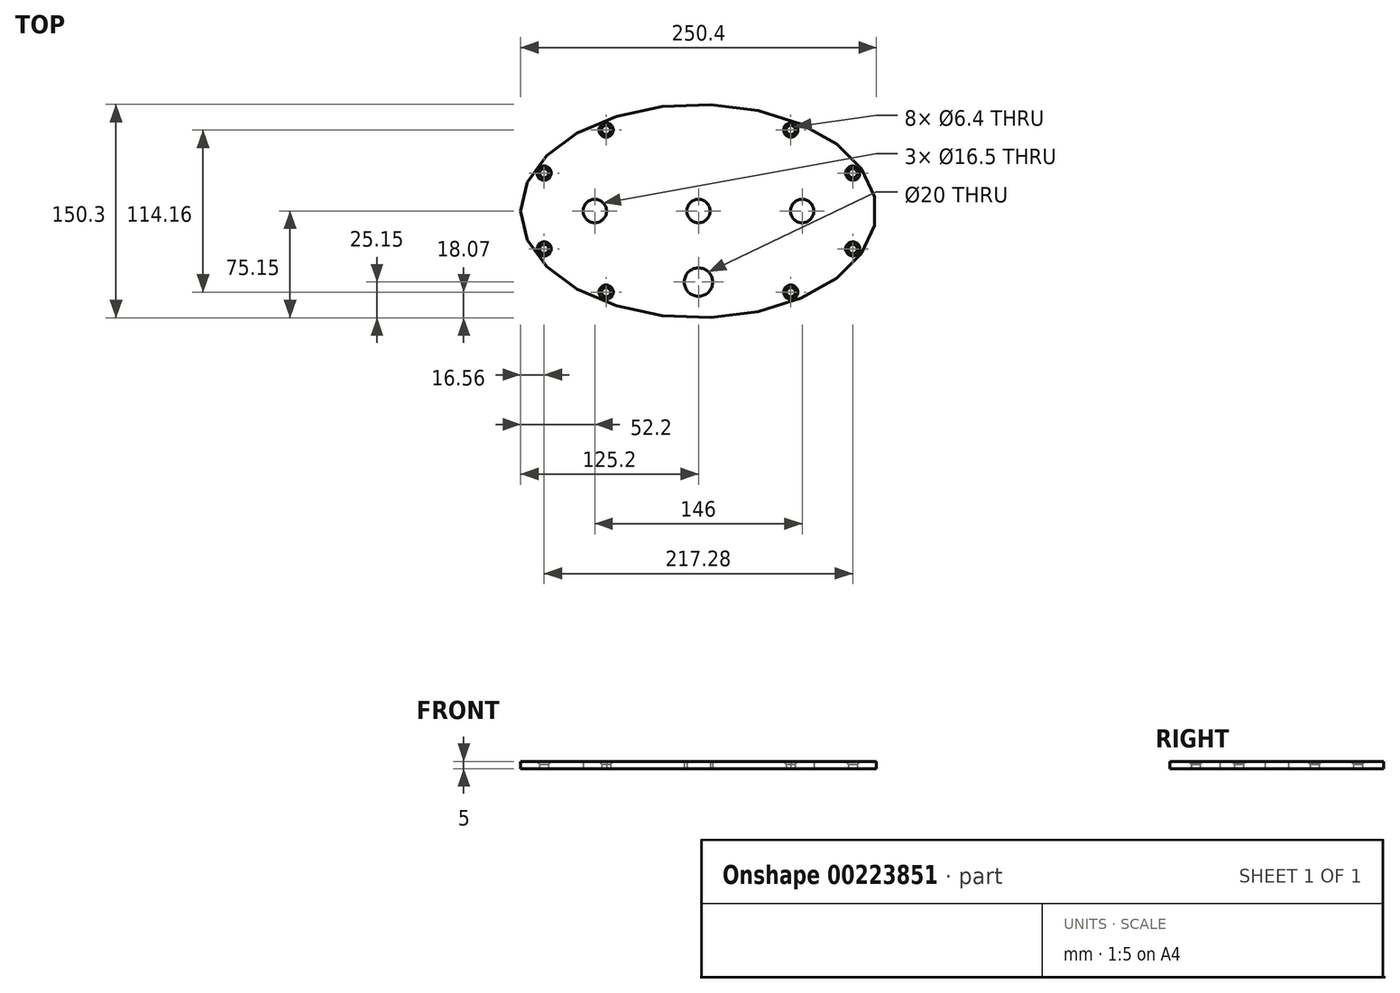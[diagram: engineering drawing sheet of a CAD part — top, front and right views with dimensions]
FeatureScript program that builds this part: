
annotation { "Feature Type Name" : "Feature", "Feature Type Description" : "" }
export const myFeature = defineFeature(function(context is Context, id is Id, definition is map)
    precondition{}
    {
        {
            var Q0;
            Q0=qCreatedBy(makeId("Top.planeOp"),FACE);
            var sketch = newSketch(context, id + "F0", { "sketchPlane" : qUnion([Q0])});
            skEllipse(sketch, "E0", {"center": v(0, 0) * mm, "majorRadius": 125.2 * mm, "minorRadius": 75.15 * mm, "majorAxis": v(-1, 0)});
            skCircle(sketch, "E1", {"center": v(0, 0) * mm, "radius": 8.25 * mm});
            skLineSegment(sketch, "E2", {"start": v(0, 0) * mm, "end": v(-73, 0) * mm});
            skCircle(sketch, "E3", {"center": v(-73, 0) * mm, "radius": 8.25 * mm});
            skCircle(sketch, "E4.MirrorC", {"center": v(73, 0) * mm, "radius": 8.25 * mm});
            skLineSegment(sketch, "E5", {"start": v(0, 0) * mm, "end": v(65, 0) * mm});
            skLineSegment(sketch, "E6", {"start": v(0, 0) * mm, "end": v(73, 0) * mm});
            skLineSegment(sketch, "E7", {"start": v(0, 0) * mm, "end": v(-50, 0) * mm});
            skLineSegment(sketch, "E8", {"start": v(0, -50) * mm, "end": v(0, -50) * mm});
            skCircle(sketch, "E9", {"center": v(0, -50) * mm, "radius": 10 * mm});
            skSolve(sketch);
        }
        {
            var Q0;
            Q0=makeQuery(id+"F0.imprint","IMPRINT",FACE,{"disambiguationData":[TD([[makeQuery(id+"F0.imprint","IMPRINT",EDGE,{"derivedFrom":sQuery(id+"F0.wireOp",EDGE,"E0")}),1.0]])]});
            extrude(context, id + "F1", {"entities" : qUnion([Q0]), "offsetDistance" : 25 * mm, "depth" : 5 * mm});
        }
        {
            var Q0;
            Q0=makeQuery(id+"F1.opExtrude","CAP_FACE",FACE,{"disambiguationData":[OSD([sQuery(id+"F0.wireOp",EDGE,"E0"),sQuery(id+"F0.wireOp",EDGE,"E1"),sQuery(id+"F0.wireOp",EDGE,"E3"),sQuery(id+"F0.wireOp",EDGE,"E4.MirrorC")])],"isStart":false});
            var sketch = newSketch(context, id + "F2", { "sketchPlane" : qUnion([Q0])});
            skLineSegment(sketch, "E10", {"start": v(-65, 0) * mm, "end": v(-65, 57.08) * mm});
            skLineSegment(sketch, "E11.MirrorCS", {"start": v(65, 0) * mm, "end": v(65, 57.08) * mm});
            skLineSegment(sketch, "E12.MirrorCS", {"start": v(65, 0) * mm, "end": v(65, -57.08) * mm});
            skLineSegment(sketch, "E13.MirrorCS", {"start": v(-65, 0) * mm, "end": v(-65, -57.08) * mm});
            skLineSegment(sketch, "E14.bottom", {"start": v(-108.64, -26.7) * mm, "end": v(108.64, -26.7) * mm});
            skLineSegment(sketch, "E14.top", {"start": v(-108.64, 26.7) * mm, "end": v(108.64, 26.7) * mm});
            skLineSegment(sketch, "E14.left", {"start": v(-108.64, -26.7) * mm, "end": v(-108.64, 26.7) * mm});
            skLineSegment(sketch, "E14.right", {"start": v(108.64, -26.7) * mm, "end": v(108.64, 26.7) * mm});
            skPoint(sketch, "E14.middle", {"position": v(0, 0) * mm});
            skSolve(sketch);
        }
        {
            var Q0;
            Q0=sQuery(id+"F2.wireOp",VERTEX,"E10.end");
            var Q1;
            Q1=sQuery(id+"F2.wireOp",VERTEX,"E11.MirrorCS.end");
            var Q2;
            Q2=sQuery(id+"F2.wireOp",VERTEX,"E12.MirrorCS.end");
            var Q3;
            Q3=sQuery(id+"F2.wireOp",VERTEX,"E13.MirrorCS.end");
            var Q4;
            Q4=sQuery(id+"F2.wireOp",VERTEX,"E14.top.end");
            var Q5;
            Q5=sQuery(id+"F2.wireOp",VERTEX,"E14.right.start");
            var Q6;
            Q6=sQuery(id+"F2.wireOp",VERTEX,"E14.left.end");
            var Q7;
            Q7=sQuery(id+"F2.wireOp",VERTEX,"E14.left.start");
            var Q8;
            Q8=makeQuery(id+"F1.opExtrude","SWEPT_BODY",BODY,{"disambiguationData":[OSD([sQuery(id+"F0.wireOp",EDGE,"E0"),sQuery(id+"F0.wireOp",EDGE,"E1"),sQuery(id+"F0.wireOp",EDGE,"E3"),sQuery(id+"F0.wireOp",EDGE,"E4.MirrorC")])]});
            hole(context, id + "F3", {"style" : HoleStyle.C_SINK, "endStyle" : HoleEndStyle.THROUGH, "holeDiameter" : 6.4 * mm, "cSinkDiameter" : 10 * mm, "cSinkAngle" : 90 * degree, "majorDiameter" : 5 * mm, "locations" : qUnion([Q0, Q1, Q2, Q3, Q4, Q5, Q6, Q7]), "scope" : qUnion([Q8]), "isTappedThrough" : true, "tappedDepth" : 12 * mm, "tapClearance" : 3, "startStyle" : HoleStartStyle.PART});
        }
    });
